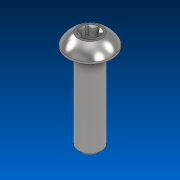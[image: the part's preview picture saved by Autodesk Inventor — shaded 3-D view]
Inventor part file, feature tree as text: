
AUTODESK INVENTOR PART (.ipt)
format: ipt  version: 2022.2 (Build 262287000, 287)  size: 182,272 bytes
history: native  units: in
note: dims shown in document units (in); Inventor stores cm internally (conversion verified against a paired STEP export)
features: direct_edit x1, chamfer x1, move_body x1
ambient origin geometry x8: Origin, YZ Plane, XZ Plane, XY Plane, X Axis, Y Axis, Z Axis, Center Point
bodies: Solid1 (feature_tree)
feature tree (3):
  direct_edit  "Direct Edit1"
  chamfer  "Chamfer2"  [1 undecoded]
  move_body  "Move1"
note: 1 required parameter value undecoded (feature->parameter linkage not recoverable at this tier; creation-order binding heuristic only, values carry confidence <= 0.55)
